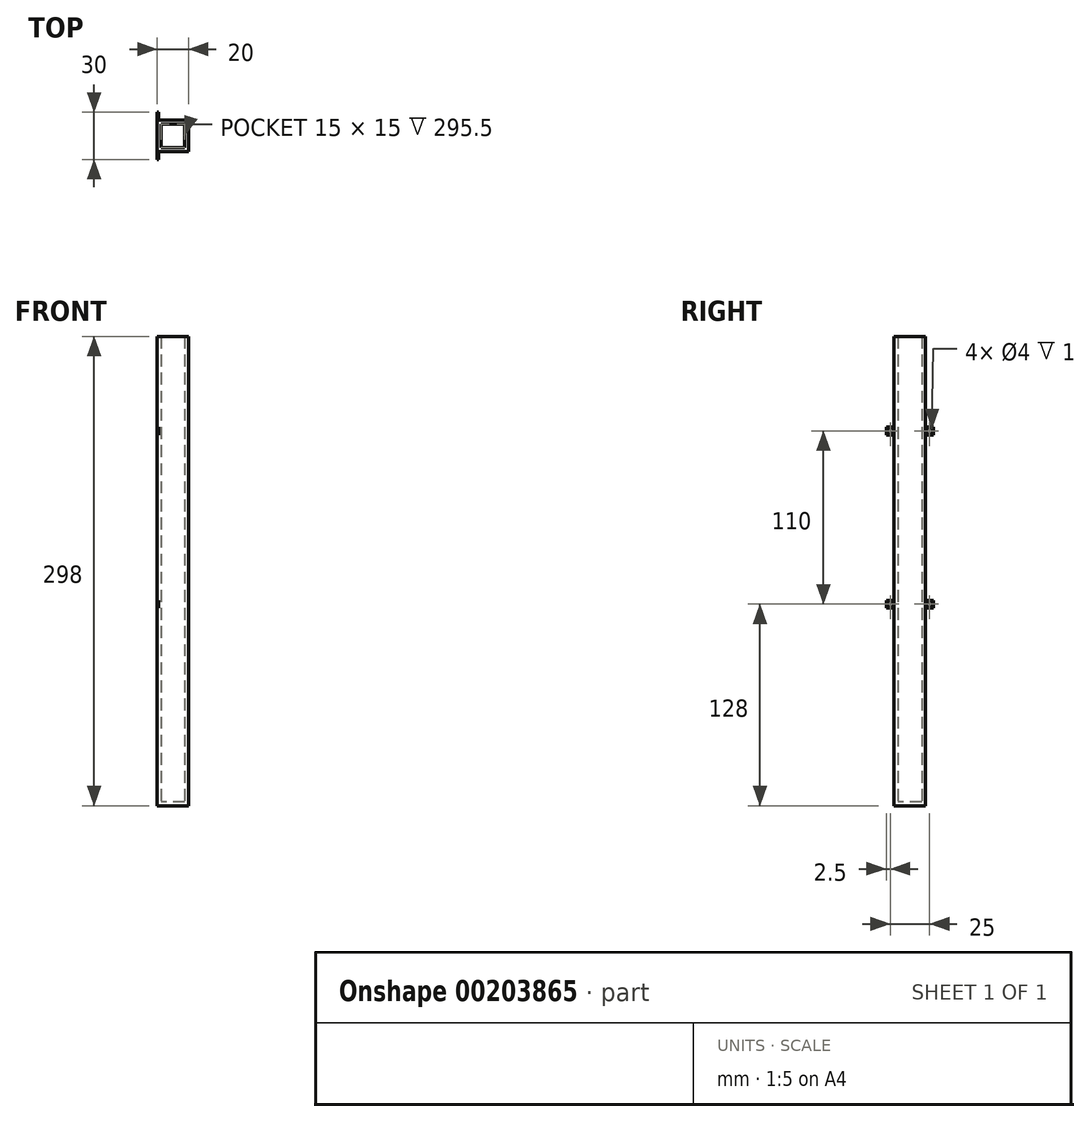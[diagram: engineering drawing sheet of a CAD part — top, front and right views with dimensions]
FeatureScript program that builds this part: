
annotation { "Feature Type Name" : "Feature", "Feature Type Description" : "" }
export const myFeature = defineFeature(function(context is Context, id is Id, definition is map)
    precondition{}
    {
        {
            var Q0;
            Q0=qCreatedBy(makeId("Right.planeOp"),FACE);
            var sketch = newSketch(context, id + "F0", { "sketchPlane" : qUnion([Q0])});
            skLineSegment(sketch, "E0.bottom", {"start": v(10, 149) * mm, "end": v(-10, 149) * mm});
            skLineSegment(sketch, "E0.top", {"start": v(10, -149) * mm, "end": v(-10, -149) * mm});
            skLineSegment(sketch, "E0.left", {"start": v(10, 149) * mm, "end": v(10, -149) * mm});
            skLineSegment(sketch, "E0.right", {"start": v(-10, 149) * mm, "end": v(-10, -149) * mm});
            skPoint(sketch, "E0.middle", {"position": v(0, 0) * mm});
            skSolve(sketch);
        }
        {
            var Q0;
            Q0 = qSketchRegion(id + "F0", true);
            extrude(context, id + "F1", {"entities" : qUnion([Q0]), "depth" : 20 * mm});
        }
        {
            var Q0;
            Q0=makeQuery(id+"F1.opExtrude","SWEPT_FACE",FACE,{"disambiguationData":[OSD([sQuery(id+"F0.wireOp",EDGE,"E0.bottom")])]});
            shell(context, id + "F2", {"entities" : qUnion([Q0]), "thickness" : 2.5 * mm});
        }
        {
            var Q0;
            Q0=makeQuery(id+"F1.opExtrude","CAP_FACE",FACE,{"disambiguationData":[OSD([sQuery(id+"F0.wireOp",EDGE,"E0.bottom"),sQuery(id+"F0.wireOp",EDGE,"E0.top"),sQuery(id+"F0.wireOp",EDGE,"E0.left"),sQuery(id+"F0.wireOp",EDGE,"E0.right")])],"isStart":true});
            var sketch = newSketch(context, id + "F3", { "sketchPlane" : qUnion([Q0])});
            skPoint(sketch, "E1.MirrorP", {"position": v(12.5, 89) * mm});
            skLineSegment(sketch, "E2.bottom", {"start": v(15, 91.5) * mm, "end": v(10, 91.5) * mm});
            skLineSegment(sketch, "E2.top", {"start": v(15, 86.5) * mm, "end": v(10, 86.5) * mm});
            skLineSegment(sketch, "E2.left", {"start": v(15, 91.5) * mm, "end": v(15, 86.5) * mm});
            skLineSegment(sketch, "E2.right", {"start": v(10, 91.5) * mm, "end": v(10, 86.5) * mm});
            skPoint(sketch, "E3.MirrorP", {"position": v(-12.5, 89) * mm});
            skLineSegment(sketch, "E4.MirrorCS", {"start": v(-15, 91.5) * mm, "end": v(-15, 86.5) * mm});
            skLineSegment(sketch, "E5.MirrorCS", {"start": v(-15, 91.5) * mm, "end": v(-10, 91.5) * mm});
            skLineSegment(sketch, "E6.MirrorCS", {"start": v(-15, 86.5) * mm, "end": v(-10, 86.5) * mm});
            skLineSegment(sketch, "E7.MirrorCS", {"start": v(-10, 91.5) * mm, "end": v(-10, 86.5) * mm});
            skCircle(sketch, "E8", {"center": v(12.5, 89) * mm, "radius": 2.5 * mm, "construction": true});
            skLineSegment(sketch, "E9", {"start": v(-26.97, 34) * mm, "end": v(38.13, 34) * mm, "construction": true});
            skLineSegment(sketch, "E10.MirrorCS", {"start": v(-15, -18.5) * mm, "end": v(-10, -18.5) * mm});
            skLineSegment(sketch, "E11.MirrorCS", {"start": v(-10, -23.5) * mm, "end": v(-10, -18.5) * mm});
            skLineSegment(sketch, "E12.MirrorCS", {"start": v(15, -18.5) * mm, "end": v(10, -18.5) * mm});
            skLineSegment(sketch, "E13.MirrorCS", {"start": v(-15, -23.5) * mm, "end": v(-15, -18.5) * mm});
            skLineSegment(sketch, "E14.MirrorCS", {"start": v(10, -23.5) * mm, "end": v(10, -18.5) * mm});
            skPoint(sketch, "E15.MirrorP", {"position": v(12.5, -21) * mm});
            skLineSegment(sketch, "E16.MirrorCS", {"start": v(-15, -23.5) * mm, "end": v(-10, -23.5) * mm});
            skPoint(sketch, "E17.MirrorP", {"position": v(-12.5, -21) * mm});
            skLineSegment(sketch, "E18.MirrorCS", {"start": v(15, -23.5) * mm, "end": v(15, -18.5) * mm});
            skLineSegment(sketch, "E19.MirrorCS", {"start": v(15, -23.5) * mm, "end": v(10, -23.5) * mm});
            skCircle(sketch, "E20.MirrorC", {"center": v(12.5, -21) * mm, "radius": 2.5 * mm, "construction": true});
            skSolve(sketch);
        }
        {
            var Q0;
            Q0 = qSketchRegion(id + "F3", true);
            extrude(context, id + "F4", {"entities" : qUnion([Q0]), "operationType" : NewBodyOperationType.ADD, "oppositeDirection" : true, "depth" : 1 * mm});
        }
        {
            var Q0;
            Q0=sQuery(id+"F3.wireOp",VERTEX,"E3.MirrorP");
            var Q1;
            Q1=sQuery(id+"F3.wireOp",VERTEX,"E1.MirrorP");
            var Q2;
            Q2=sQuery(id+"F3.wireOp",VERTEX,"39ebcd25-47dd-4b05-a139-5e344c83ebe31.MirrorP");
            var Q3;
            Q3=sQuery(id+"F3.wireOp",VERTEX,"39ebcd25-47dd-4b05-a139-5e344c83ebe311.MirrorP");
            var Q4;
            Q4=sQuery(id+"F3.wireOp",VERTEX,"E17.MirrorP");
            var Q5;
            Q5=sQuery(id+"F3.wireOp",VERTEX,"E15.MirrorP");
            var Q6;
            Q6=makeQuery(id+"F1.opExtrude","SWEPT_BODY",BODY,{"disambiguationData":[OSD([sQuery(id+"F0.wireOp",EDGE,"E0.bottom"),sQuery(id+"F0.wireOp",EDGE,"E0.top"),sQuery(id+"F0.wireOp",EDGE,"E0.left"),sQuery(id+"F0.wireOp",EDGE,"E0.right")])]});
            hole(context, id + "F5", {"style" : HoleStyle.SIMPLE, "endStyle" : HoleEndStyle.THROUGH, "holeDiameter" : 4 * mm, "locations" : qUnion([Q0, Q1, Q2, Q3, Q4, Q5]), "scope" : qUnion([Q6]), "isTappedThrough" : true});
        }
    });
